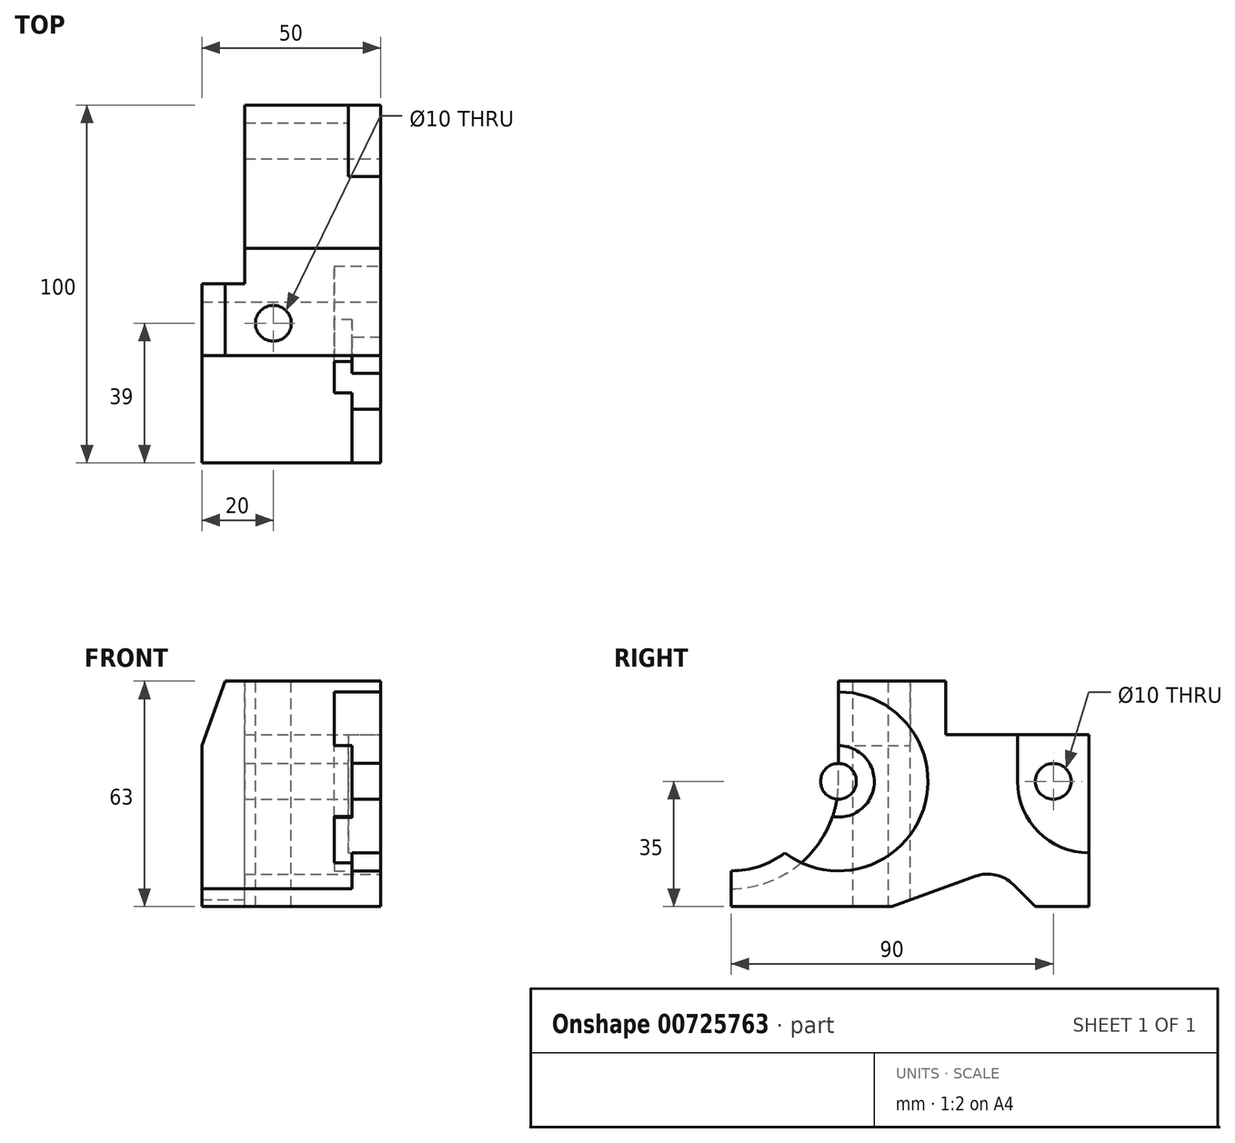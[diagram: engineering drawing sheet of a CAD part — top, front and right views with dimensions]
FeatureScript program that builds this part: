
annotation { "Feature Type Name" : "Feature", "Feature Type Description" : "" }
export const myFeature = defineFeature(function(context is Context, id is Id, definition is map)
    precondition{}
    {
        {
            var Q0;
            Q0=qCreatedBy(makeId("Right.planeOp"),FACE);
            var sketch = newSketch(context, id + "F0", { "sketchPlane" : qUnion([Q0])});
            skLineSegment(sketch, "E0.bottom", {"start": v(0, 0) * mm, "end": v(100, 0) * mm});
            skLineSegment(sketch, "E0.top", {"start": v(0, 63) * mm, "end": v(100, 63) * mm});
            skLineSegment(sketch, "E0.left", {"start": v(0, 0) * mm, "end": v(0, 63) * mm});
            skLineSegment(sketch, "E0.right", {"start": v(100, 0) * mm, "end": v(100, 63) * mm});
            skSolve(sketch);
        }
        {
            var Q0;
            Q0 = qSketchRegion(id + "F0", true);
            extrude(context, id + "F1", {"entities" : qUnion([Q0]), "depth" : 50 * mm, "offsetDistance" : 25 * mm});
        }
        {
            var Q0;
            Q0=makeQuery(id+"F1.opExtrude","CAP_FACE",FACE,{"disambiguationData":[OSD([sQuery(id+"F0.wireOp",EDGE,"E0.bottom"),sQuery(id+"F0.wireOp",EDGE,"E0.top"),sQuery(id+"F0.wireOp",EDGE,"E0.left"),sQuery(id+"F0.wireOp",EDGE,"E0.right")])],"isStart":false});
            var sketch = newSketch(context, id + "F2", { "sketchPlane" : qUnion([Q0])});
            skLineSegment(sketch, "E1.bottom", {"start": v(100, 63) * mm, "end": v(60, 63) * mm});
            skLineSegment(sketch, "E1.top", {"start": v(100, 48) * mm, "end": v(60, 48) * mm});
            skLineSegment(sketch, "E1.left", {"start": v(100, 63) * mm, "end": v(100, 48) * mm});
            skLineSegment(sketch, "E1.right", {"start": v(60, 63) * mm, "end": v(60, 48) * mm});
            skSolve(sketch);
        }
        {
            var Q0;
            Q0 = qSketchRegion(id + "F2", true);
            extrude(context, id + "F3", {"entities" : qUnion([Q0]), "operationType" : NewBodyOperationType.REMOVE, "endBound" : BoundingType.THROUGH_ALL, "oppositeDirection" : true, "depth" : 25 * mm, "offsetDistance" : 25 * mm});
        }
        {
            var Q0;
            Q0=makeQuery(id+"F1.opExtrude","CAP_FACE",FACE,{"disambiguationData":[OSD([sQuery(id+"F0.wireOp",EDGE,"E0.bottom"),sQuery(id+"F0.wireOp",EDGE,"E0.top"),sQuery(id+"F0.wireOp",EDGE,"E0.left"),sQuery(id+"F0.wireOp",EDGE,"E0.right")])],"isStart":false});
            var sketch = newSketch(context, id + "F4", { "sketchPlane" : qUnion([Q0])});
            skLineSegment(sketch, "E2", {"start": v(80, 48) * mm, "end": v(80, 35) * mm});
            skArc(sketch, "E3", {"start": v(80, 35) * mm, "mid": v(85.86, 20.86) * mm, "end": v(100, 15) * mm});
            skLineSegment(sketch, "E4", {"start": v(80, 48) * mm, "end": v(100, 48) * mm});
            skLineSegment(sketch, "E5", {"start": v(100, 48) * mm, "end": v(100, 15) * mm});
            skSolve(sketch);
        }
        {
            var Q0;
            Q0 = qSketchRegion(id + "F4", true);
            extrude(context, id + "F5", {"entities" : qUnion([Q0]), "operationType" : NewBodyOperationType.REMOVE, "oppositeDirection" : true, "depth" : 9 * mm, "offsetDistance" : 25 * mm});
        }
        {
            var Q0;
            Q0=makeQuery(id+"F1.opExtrude","CAP_FACE",FACE,{"disambiguationData":[OSD([sQuery(id+"F0.wireOp",EDGE,"E0.bottom"),sQuery(id+"F0.wireOp",EDGE,"E0.top"),sQuery(id+"F0.wireOp",EDGE,"E0.left"),sQuery(id+"F0.wireOp",EDGE,"E0.right")])],"isStart":false});
            var sketch = newSketch(context, id + "F6", { "sketchPlane" : qUnion([Q0])});
            skLineSegment(sketch, "E6", {"start": v(45, 0) * mm, "end": v(68.34, 8.5) * mm});
            skLineSegment(sketch, "E7", {"start": v(85, 0) * mm, "end": v(78.83, 6.17) * mm});
            skArc(sketch, "E8", {"start": v(68.34, 8.5) * mm, "mid": v(73.92, 8.86) * mm, "end": v(78.83, 6.17) * mm});
            skLineSegment(sketch, "E9", {"start": v(45, 0) * mm, "end": v(85, 0) * mm});
            skSolve(sketch);
        }
        {
            var Q0;
            Q0 = qSketchRegion(id + "F6", true);
            extrude(context, id + "F7", {"entities" : qUnion([Q0]), "operationType" : NewBodyOperationType.REMOVE, "endBound" : BoundingType.THROUGH_ALL, "oppositeDirection" : true, "depth" : 25 * mm, "offsetDistance" : 25 * mm});
        }
        {
            var Q0;
            Q0=makeQuery(id+"F1.opExtrude","CAP_FACE",FACE,{"disambiguationData":[OSD([sQuery(id+"F0.wireOp",EDGE,"E0.bottom"),sQuery(id+"F0.wireOp",EDGE,"E0.top"),sQuery(id+"F0.wireOp",EDGE,"E0.left"),sQuery(id+"F0.wireOp",EDGE,"E0.right")])],"isStart":false});
            var sketch = newSketch(context, id + "F8", { "sketchPlane" : qUnion([Q0])});
            skCircle(sketch, "E10", {"center": v(30, 35) * mm, "radius": 25 * mm});
            skSolve(sketch);
        }
        {
            var Q0;
            Q0 = qSketchRegion(id + "F8", true);
            extrude(context, id + "F9", {"entities" : qUnion([Q0]), "operationType" : NewBodyOperationType.REMOVE, "oppositeDirection" : true, "depth" : 13 * mm, "offsetDistance" : 25 * mm});
        }
        {
            var Q0;
            Q0=makeQuery(id+"F9.boolean.opBoolean","COPY",FACE,{"derivedFrom":makeQuery(id+"F9.opExtrude","CAP_FACE",FACE,{"disambiguationData":[OSD([sQuery(id+"F8.wireOp",EDGE,"E10")])],"isStart":false})});
            var sketch = newSketch(context, id + "F10", { "sketchPlane" : qUnion([Q0])});
            skCircle(sketch, "E11", {"center": v(30, 35) * mm, "radius": 10 * mm});
            skSolve(sketch);
        }
        {
            var Q0;
            Q0 = qSketchRegion(id + "F10", true);
            extrude(context, id + "F11", {"entities" : qUnion([Q0]), "operationType" : NewBodyOperationType.ADD, "depth" : 5 * mm, "offsetDistance" : 25 * mm});
        }
        {
            var Q0;
            Q0=makeQuery(id+"F11.opExtrude","CAP_FACE",FACE,{"disambiguationData":[OSD([sQuery(id+"F10.wireOp",EDGE,"E11")])],"isStart":false});
            var sketch = newSketch(context, id + "F12", { "sketchPlane" : qUnion([Q0])});
            skCircle(sketch, "E12", {"center": v(30, 35) * mm, "radius": 5 * mm});
            skSolve(sketch);
        }
        {
            var Q0;
            Q0 = qSketchRegion(id + "F12", true);
            extrude(context, id + "F13", {"entities" : qUnion([Q0]), "operationType" : NewBodyOperationType.ADD, "depth" : 8 * mm, "offsetDistance" : 25 * mm});
        }
        {
            var Q0;
            Q0=makeQuery(id+"F1.opExtrude","CAP_FACE",FACE,{"disambiguationData":[OSD([sQuery(id+"F0.wireOp",EDGE,"E0.bottom"),sQuery(id+"F0.wireOp",EDGE,"E0.top"),sQuery(id+"F0.wireOp",EDGE,"E0.left"),sQuery(id+"F0.wireOp",EDGE,"E0.right")])],"isStart":false});
            var sketch = newSketch(context, id + "F14", { "sketchPlane" : qUnion([Q0])});
            skArc(sketch, "E13", {"start": v(25, 35) * mm, "mid": v(17.68, 17.32) * mm, "end": v(0, 10) * mm});
            skLineSegment(sketch, "E14", {"start": v(25, 35) * mm, "end": v(25, 63) * mm});
            skLineSegment(sketch, "E15", {"start": v(25, 63) * mm, "end": v(0, 63) * mm});
            skLineSegment(sketch, "E16", {"start": v(0, 63) * mm, "end": v(0, 10) * mm});
            skSolve(sketch);
        }
        {
            var Q0;
            Q0 = qSketchRegion(id + "F14", true);
            extrude(context, id + "F15", {"entities" : qUnion([Q0]), "operationType" : NewBodyOperationType.REMOVE, "endBound" : BoundingType.THROUGH_ALL, "oppositeDirection" : true, "depth" : 25 * mm, "offsetDistance" : 25 * mm});
        }
        {
            var Q0;
            Q0=makeQuery(id+"F1.opExtrude","CAP_FACE",FACE,{"disambiguationData":[OSD([sQuery(id+"F0.wireOp",EDGE,"E0.bottom"),sQuery(id+"F0.wireOp",EDGE,"E0.top"),sQuery(id+"F0.wireOp",EDGE,"E0.left"),sQuery(id+"F0.wireOp",EDGE,"E0.right")])],"isStart":true});
            var sketch = newSketch(context, id + "F16", { "sketchPlane" : qUnion([Q0])});
            skArc(sketch, "E17", {"start": v(-30, 35) * mm, "mid": v(-21.21, 13.79) * mm, "end": v(0, 5) * mm});
            skLineSegment(sketch, "E18", {"start": v(-30, 35) * mm, "end": v(-30, 63) * mm});
            skLineSegment(sketch, "E19", {"start": v(-30, 63) * mm, "end": v(0, 63) * mm});
            skLineSegment(sketch, "E20", {"start": v(0, 63) * mm, "end": v(0, 5) * mm});
            skSolve(sketch);
        }
        {
            var Q0;
            Q0 = qSketchRegion(id + "F16", true);
            extrude(context, id + "F17", {"entities" : qUnion([Q0]), "operationType" : NewBodyOperationType.REMOVE, "oppositeDirection" : true, "depth" : 42 * mm, "offsetDistance" : 25 * mm});
        }
        {
            var Q0;
            Q0=makeQuery(id+"F5.boolean.opBoolean","COPY",FACE,{"derivedFrom":makeQuery(id+"F5.opExtrude","CAP_FACE",FACE,{"disambiguationData":[OSD([sQuery(id+"F4.wireOp",EDGE,"E2"),sQuery(id+"F4.wireOp",EDGE,"E3"),sQuery(id+"F4.wireOp",EDGE,"E4"),sQuery(id+"F4.wireOp",EDGE,"E5")])],"isStart":false})});
            var sketch = newSketch(context, id + "F18", { "sketchPlane" : qUnion([Q0])});
            skCircle(sketch, "E21", {"center": v(90, 35) * mm, "radius": 5 * mm});
            skSolve(sketch);
        }
        {
            var Q0;
            Q0 = qSketchRegion(id + "F18", true);
            extrude(context, id + "F19", {"entities" : qUnion([Q0]), "operationType" : NewBodyOperationType.REMOVE, "endBound" : BoundingType.THROUGH_ALL, "oppositeDirection" : true, "depth" : 25 * mm, "offsetDistance" : 25 * mm});
        }
        {
            var Q0;
            Q0=makeQuery(id+"F1.opExtrude","SWEPT_FACE",FACE,{"disambiguationData":[OSD([sQuery(id+"F0.wireOp",EDGE,"E0.top")])]});
            var sketch = newSketch(context, id + "F20", { "sketchPlane" : qUnion([Q0])});
            skLineSegment(sketch, "E22.bottom", {"start": v(0, 100) * mm, "end": v(12, 100) * mm});
            skLineSegment(sketch, "E22.top", {"start": v(0, 50) * mm, "end": v(12, 50) * mm});
            skLineSegment(sketch, "E22.left", {"start": v(0, 100) * mm, "end": v(0, 50) * mm});
            skLineSegment(sketch, "E22.right", {"start": v(12, 100) * mm, "end": v(12, 50) * mm});
            skSolve(sketch);
        }
        {
            var Q0;
            Q0 = qSketchRegion(id + "F20", true);
            extrude(context, id + "F21", {"entities" : qUnion([Q0]), "operationType" : NewBodyOperationType.REMOVE, "endBound" : BoundingType.THROUGH_ALL, "oppositeDirection" : true, "depth" : 25 * mm, "offsetDistance" : 25 * mm});
        }
        {
            var Q0;
            Q0=makeQuery(id+"F1.opExtrude","SWEPT_FACE",FACE,{"disambiguationData":[OSD([sQuery(id+"F0.wireOp",EDGE,"E0.top")])]});
            var sketch = newSketch(context, id + "F22", { "sketchPlane" : qUnion([Q0])});
            skCircle(sketch, "E23", {"center": v(20, 39) * mm, "radius": 5 * mm});
            skSolve(sketch);
        }
        {
            var Q0;
            Q0 = qSketchRegion(id + "F22", true);
            extrude(context, id + "F23", {"entities" : qUnion([Q0]), "operationType" : NewBodyOperationType.REMOVE, "endBound" : BoundingType.THROUGH_ALL, "oppositeDirection" : true, "depth" : 25 * mm, "offsetDistance" : 25 * mm});
        }
        {
            var Q0;
            Q0=makeQuery(id+"F21.boolean.opBoolean","COPY",FACE,{"derivedFrom":makeQuery(id+"F21.opExtrude","SWEPT_FACE",FACE,{"disambiguationData":[OSD([sQuery(id+"F20.wireOp",EDGE,"E22.top")])]})});
            var sketch = newSketch(context, id + "F24", { "sketchPlane" : qUnion([Q0])});
            skLineSegment(sketch, "E24", {"start": v(0, 63) * mm, "end": v(-6.55, 63) * mm});
            skLineSegment(sketch, "E25", {"start": v(-6.55, 63) * mm, "end": v(0, 45) * mm});
            skLineSegment(sketch, "E26", {"start": v(0, 45) * mm, "end": v(0, 63) * mm});
            skSolve(sketch);
        }
        {
            var Q0;
            Q0 = qSketchRegion(id + "F24", true);
            extrude(context, id + "F25", {"entities" : qUnion([Q0]), "operationType" : NewBodyOperationType.REMOVE, "endBound" : BoundingType.THROUGH_ALL, "oppositeDirection" : true, "depth" : 25 * mm, "offsetDistance" : 25 * mm});
        }
        {
            var Q0;
            Q0=makeQuery(id+"F1.opExtrude","CAP_FACE",FACE,{"disambiguationData":[OSD([sQuery(id+"F0.wireOp",EDGE,"E0.bottom"),sQuery(id+"F0.wireOp",EDGE,"E0.top"),sQuery(id+"F0.wireOp",EDGE,"E0.left"),sQuery(id+"F0.wireOp",EDGE,"E0.right")])],"isStart":false});
            var sketch = newSketch(context, id + "F26", { "sketchPlane" : qUnion([Q0])});
            skLineSegment(sketch, "E27", {"start": v(25, 63) * mm, "end": v(30, 63) * mm});
            skLineSegment(sketch, "E28", {"start": v(30, 63) * mm, "end": v(30, 59) * mm});
            skLineSegment(sketch, "E29", {"start": v(30, 59) * mm, "end": v(25, 59) * mm});
            skLineSegment(sketch, "E30", {"start": v(25, 59) * mm, "end": v(25, 63) * mm});
            skSolve(sketch);
        }
        {
            var Q0;
            Q0 = qSketchRegion(id + "F26", true);
            extrude(context, id + "F27", {"entities" : qUnion([Q0]), "operationType" : NewBodyOperationType.REMOVE, "endBound" : BoundingType.THROUGH_ALL, "oppositeDirection" : true, "depth" : 25 * mm, "offsetDistance" : 25 * mm});
        }
    });
